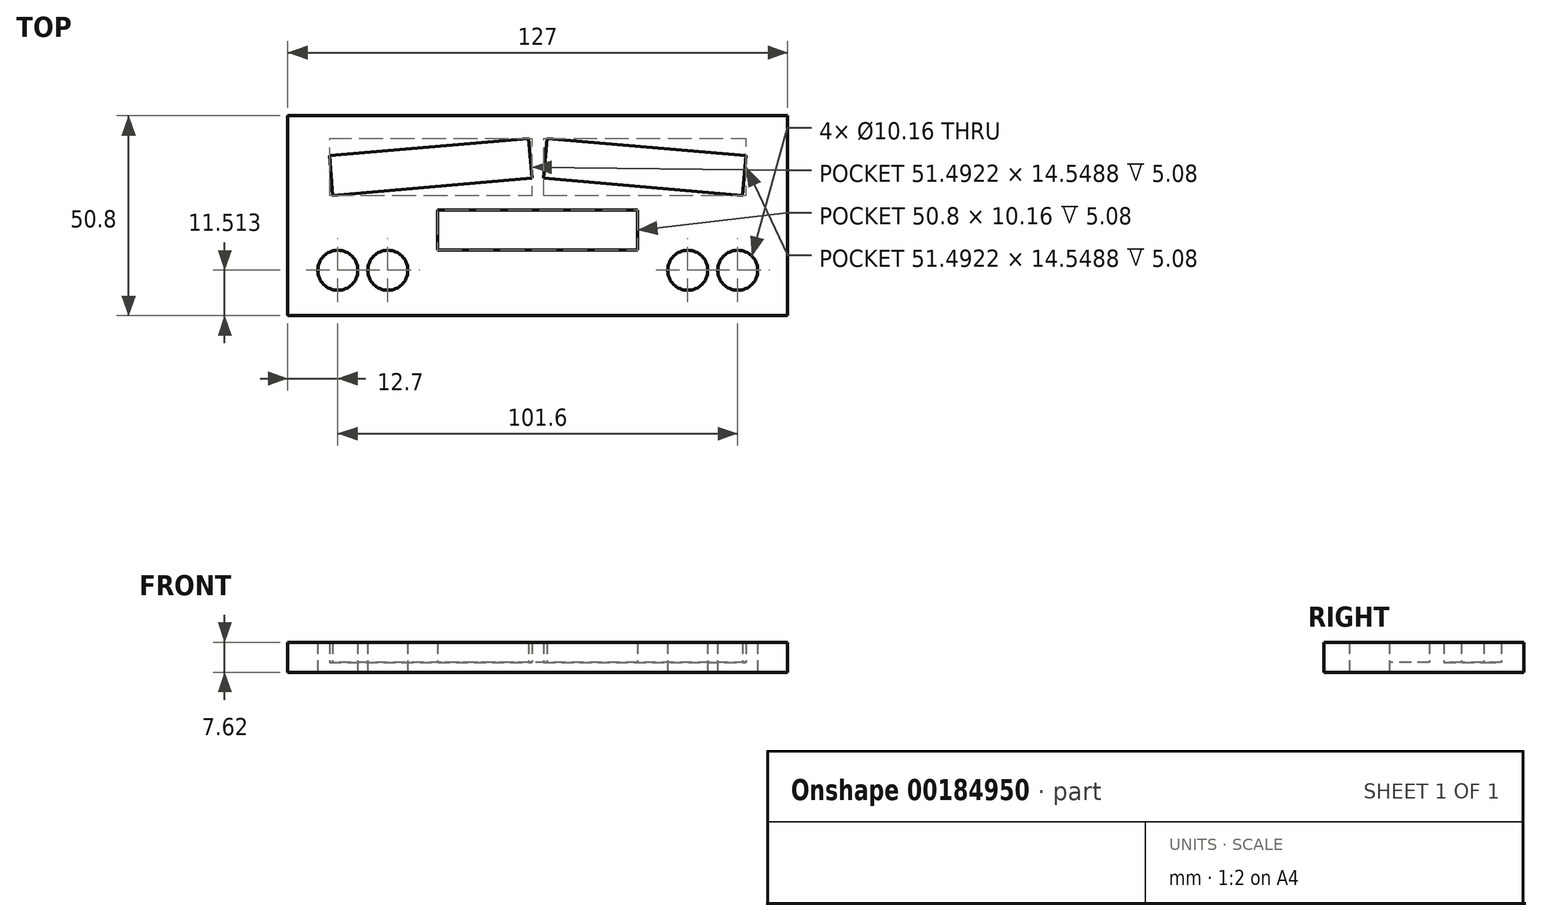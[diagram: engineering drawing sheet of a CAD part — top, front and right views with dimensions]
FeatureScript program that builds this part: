
annotation { "Feature Type Name" : "Feature", "Feature Type Description" : "" }
export const myFeature = defineFeature(function(context is Context, id is Id, definition is map)
    precondition{}
    {
        {
            var Q0;
            Q0=qCreatedBy(makeId("Top.planeOp"),FACE);
            var sketch = newSketch(context, id + "F0", { "sketchPlane" : qUnion([Q0])});
            skLineSegment(sketch, "E0.bottom", {"start": v(-63.5, 20.32) * mm, "end": v(63.5, 20.32) * mm});
            skLineSegment(sketch, "E0.top", {"start": v(-63.5, -30.48) * mm, "end": v(63.5, -30.48) * mm});
            skLineSegment(sketch, "E0.left", {"start": v(-63.5, 20.32) * mm, "end": v(-63.5, -30.48) * mm});
            skLineSegment(sketch, "E0.right", {"start": v(63.5, 20.32) * mm, "end": v(63.5, -30.48) * mm});
            skLineSegment(sketch, "E1.bottom", {"start": v(0, 0) * mm, "end": v(-63.5, 0) * mm, "construction": true});
            skLineSegment(sketch, "E1.top", {"start": v(0, 20.32) * mm, "end": v(-63.5, 20.32) * mm});
            skLineSegment(sketch, "E1.left", {"start": v(0, 0) * mm, "end": v(0, 20.32) * mm, "construction": true});
            skLineSegment(sketch, "E1.right", {"start": v(-63.5, 0) * mm, "end": v(-63.5, 20.32) * mm});
            skLineSegment(sketch, "E2.bottom", {"start": v(0, 0) * mm, "end": v(63.5, 0) * mm, "construction": true});
            skLineSegment(sketch, "E2.top", {"start": v(0, -30.48) * mm, "end": v(63.5, -30.48) * mm});
            skLineSegment(sketch, "E2.left", {"start": v(0, 0) * mm, "end": v(0, -30.48) * mm, "construction": true});
            skLineSegment(sketch, "E2.right", {"start": v(63.5, 0) * mm, "end": v(63.5, -30.48) * mm});
            skLineSegment(sketch, "E3", {"start": v(-31.75, 0) * mm, "end": v(-31.75, 20.32) * mm, "construction": true});
            skLineSegment(sketch, "E4", {"start": v(31.75, 0) * mm, "end": v(31.75, 20.32) * mm, "construction": true});
            skLineSegment(sketch, "E5", {"start": v(-31.75, 0) * mm, "end": v(-63.5, 0) * mm, "construction": true});
            skLineSegment(sketch, "E6", {"start": v(31.75, 0) * mm, "end": v(63.5, 0) * mm, "construction": true});
            skLineSegment(sketch, "E7", {"start": v(-52.07, 0) * mm, "end": v(-52.96, 10.12) * mm});
            skLineSegment(sketch, "E8", {"start": v(-52.96, 10.12) * mm, "end": v(-2.35, 14.55) * mm});
            skLineSegment(sketch, "E9", {"start": v(-2.35, 14.55) * mm, "end": v(-1.46, 4.43) * mm});
            skLineSegment(sketch, "E10", {"start": v(-1.46, 4.43) * mm, "end": v(-52.07, 0) * mm});
            skLineSegment(sketch, "E11.bottom", {"start": v(25.4, -3.73) * mm, "end": v(-25.4, -3.73) * mm});
            skLineSegment(sketch, "E11.top", {"start": v(25.4, -13.89) * mm, "end": v(-25.4, -13.89) * mm});
            skLineSegment(sketch, "E11.left", {"start": v(25.4, -3.73) * mm, "end": v(25.4, -13.89) * mm});
            skLineSegment(sketch, "E11.right", {"start": v(-25.4, -3.73) * mm, "end": v(-25.4, -13.89) * mm});
            skPoint(sketch, "E11.middle", {"position": v(0, -8.8) * mm});
            skCircle(sketch, "E12", {"center": v(-50.8, -18.97) * mm, "radius": 5.08 * mm});
            skCircle(sketch, "E13", {"center": v(50.8, -18.97) * mm, "radius": 5.08 * mm});
            skCircle(sketch, "E14", {"center": v(38.1, -18.97) * mm, "radius": 5.08 * mm});
            skCircle(sketch, "E15", {"center": v(-38.1, -18.97) * mm, "radius": 5.08 * mm});
            skLineSegment(sketch, "E16", {"start": v(-63.5, -18.97) * mm, "end": v(63.5, -18.97) * mm});
            skLineSegment(sketch, "E17.MirrorCS", {"start": v(52.96, 10.12) * mm, "end": v(2.35, 14.55) * mm});
            skLineSegment(sketch, "E18.MirrorCS", {"start": v(2.35, 14.55) * mm, "end": v(1.46, 4.43) * mm});
            skLineSegment(sketch, "E19.MirrorCS", {"start": v(1.46, 4.43) * mm, "end": v(52.07, 0) * mm});
            skLineSegment(sketch, "E20.MirrorCS", {"start": v(52.07, 0) * mm, "end": v(52.96, 10.12) * mm});
            skSolve(sketch);
        }
        {
            var Q0;
            Q0 = qSketchRegion(id + "F0", true);
            extrude(context, id + "F1", {"entities" : qUnion([Q0]), "depth" : 7.62 * mm});
        }
        {
            var Q0;
            Q0=makeQuery(id+"F0.imprint","IMPRINT",FACE,{"disambiguationData":[TD([[makeQuery(id+"F0.imprint","IMPRINT",EDGE,{"derivedFrom":sQuery(id+"F0.wireOp",EDGE,"E11.bottom")}),1.0]])]});
            var Q1;
            Q1=makeQuery(id+"F0.imprint","IMPRINT",FACE,{"disambiguationData":[TD([[makeQuery(id+"F0.imprint","IMPRINT",EDGE,{"derivedFrom":sQuery(id+"F0.wireOp",EDGE,"E7")}),-1.0]])]});
            var Q2;
            Q2=makeQuery(id+"F0.imprint","IMPRINT",FACE,{"disambiguationData":[TD([[makeQuery(id+"F0.imprint","IMPRINT",EDGE,{"derivedFrom":sQuery(id+"F0.wireOp",EDGE,"E17.MirrorCS")}),1.0]])]});
            extrude(context, id + "F2", {"entities" : qUnion([Q0, Q1, Q2]), "operationType" : NewBodyOperationType.ADD, "depth" : 2.54 * mm});
        }
    });
